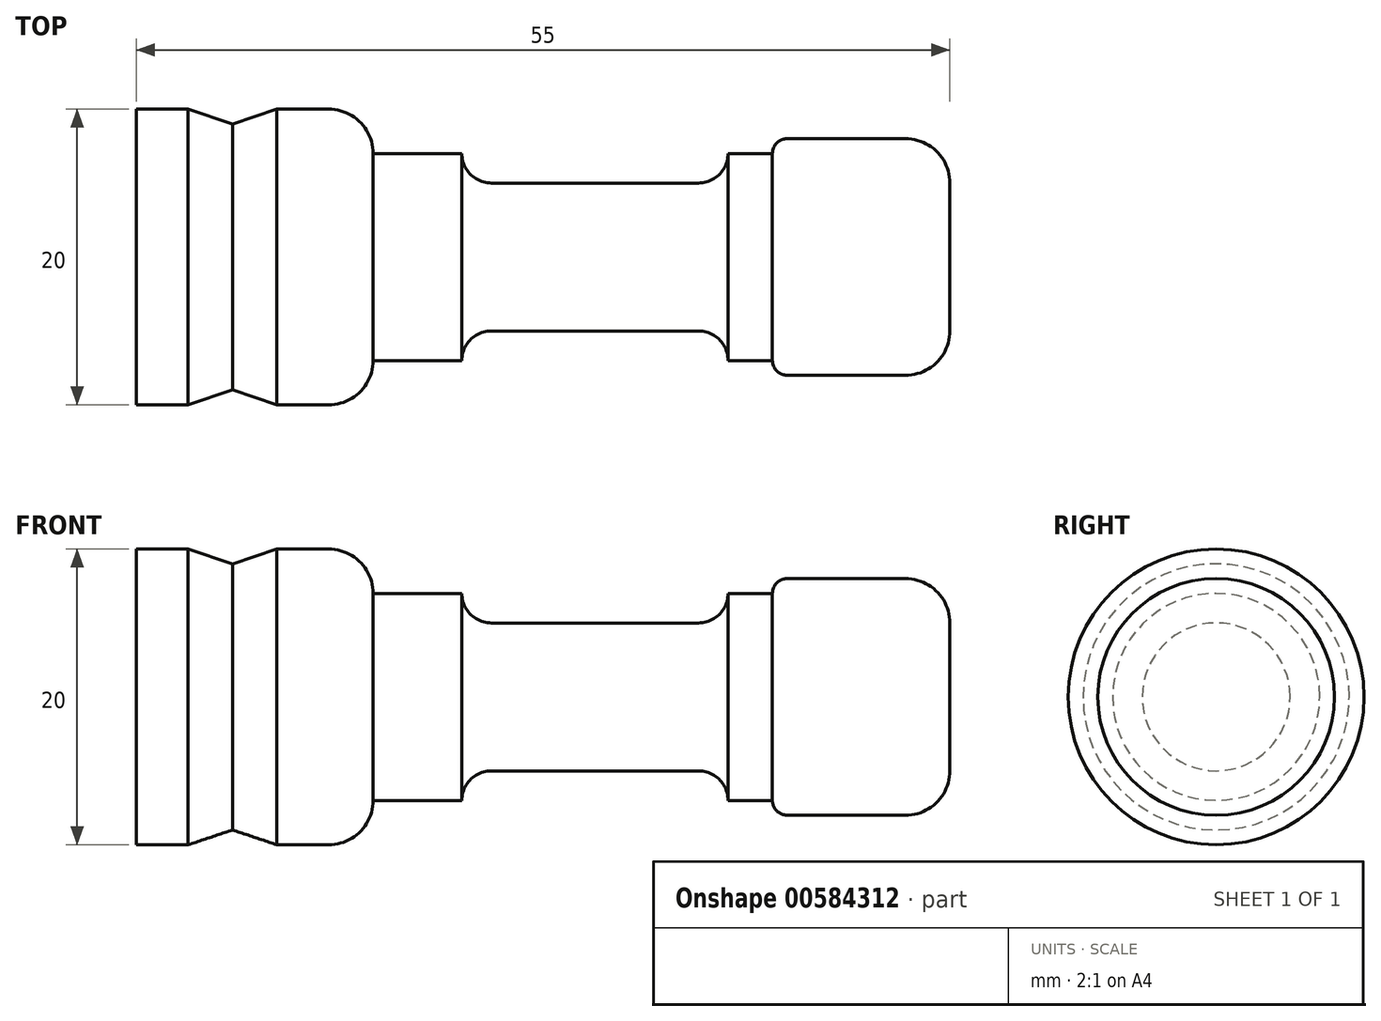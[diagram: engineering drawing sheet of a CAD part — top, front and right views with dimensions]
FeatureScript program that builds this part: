
annotation { "Feature Type Name" : "Feature", "Feature Type Description" : "" }
export const myFeature = defineFeature(function(context is Context, id is Id, definition is map)
    precondition{}
    {
        {
            var Q0;
            Q0=qCreatedBy(makeId("Front.planeOp"),FACE);
            var sketch = newSketch(context, id + "F0", { "sketchPlane" : qUnion([Q0])});
            skLineSegment(sketch, "E0", {"start": v(0, 0) * mm, "end": v(55, 0) * mm});
            skLineSegment(sketch, "E1", {"start": v(0, 0) * mm, "end": v(0, -10) * mm});
            skLineSegment(sketch, "E2", {"start": v(0, -10) * mm, "end": v(3.5, -10) * mm});
            skLineSegment(sketch, "E3", {"start": v(3.5, -10) * mm, "end": v(6.5, -9) * mm});
            skLineSegment(sketch, "E4", {"start": v(9.5, -10) * mm, "end": v(6.5, -9) * mm});
            skLineSegment(sketch, "E5", {"start": v(55, 0) * mm, "end": v(55, -5) * mm});
            skLineSegment(sketch, "E6", {"start": v(52, -8) * mm, "end": v(44, -8) * mm});
            skLineSegment(sketch, "E7", {"start": v(43, -7) * mm, "end": v(43, -7) * mm});
            skLineSegment(sketch, "E8", {"start": v(43, -7) * mm, "end": v(40, -7) * mm});
            skLineSegment(sketch, "E9", {"start": v(40, -7) * mm, "end": v(40, -7) * mm});
            skLineSegment(sketch, "E10", {"start": v(38, -5) * mm, "end": v(24, -5) * mm});
            skLineSegment(sketch, "E11", {"start": v(22, -7) * mm, "end": v(22, -7) * mm});
            skLineSegment(sketch, "E12", {"start": v(22, -7) * mm, "end": v(16, -7) * mm});
            skLineSegment(sketch, "E13", {"start": v(16, -7) * mm, "end": v(16, -7) * mm});
            skLineSegment(sketch, "E14", {"start": v(13, -10) * mm, "end": v(9.5, -10) * mm});
            skPoint(sketch, "E15.visualSharp", {"position": v(55, -8) * mm});
            skArc(sketch, "E15.filletArc", {"start": v(52, -8) * mm, "mid": v(54.12, -7.12) * mm, "end": v(55, -5) * mm});
            skPoint(sketch, "E16.visualSharp", {"position": v(43, -8) * mm});
            skArc(sketch, "E16.filletArc", {"start": v(43, -7) * mm, "mid": v(43.3, -7.7) * mm, "end": v(44, -8) * mm});
            skPoint(sketch, "E17.visualSharp", {"position": v(40, -5) * mm});
            skArc(sketch, "E17.filletArc", {"start": v(40, -7) * mm, "mid": v(39.41, -5.59) * mm, "end": v(38, -5) * mm});
            skPoint(sketch, "E18.visualSharp", {"position": v(22, -5) * mm});
            skArc(sketch, "E18.filletArc", {"start": v(24, -5) * mm, "mid": v(22.59, -5.59) * mm, "end": v(22, -7) * mm});
            skPoint(sketch, "E19.visualSharp", {"position": v(16, -10) * mm});
            skArc(sketch, "E19.filletArc", {"start": v(13, -10) * mm, "mid": v(15.12, -9.12) * mm, "end": v(16, -7) * mm});
            skLineSegment(sketch, "E20", {"start": v(55, 0) * mm, "end": v(-5.18, 0) * mm, "construction": true});
            skSolve(sketch);
        }
        {
            var Q0;
            Q0=makeQuery(id+"F0.imprint","IMPRINT",FACE,{"disambiguationData":[TD([[makeQuery(id+"F0.imprint","IMPRINT",EDGE,{"derivedFrom":sQuery(id+"F0.wireOp",EDGE,"E0")}),-1.0]])]});
            var Q1;
            Q1=sQuery(id+"F0.wireOp",EDGE,"E20");
            revolve(context, id + "F1", {"entities" : qUnion([Q0]), "axis" : qUnion([Q1]), "revolveType" : RevolveType.FULL});
        }
    });
